# Revit family: NBS_WallgateLtd_WlHngUrnls_CWU-01
name_source: partatom
category: Plumbing Fixtures
revit_build: Autodesk Revit 2014 (Build: 20130709_2115(x64)
units: mm (PartAtom-declared; Revit-internal decimal feet)

## types (1)
- CWU-01
    AssetType = Fixed
    BIMObjectName = NBS_WallgateLtd_WallHungWashUrinal_CWU-01
    BowlUrinalMaterial = NBS_Concept
    ColourOptions = MA - Thames, MAH - Frost, MAW - White, MC - Bluestone, MCA - Aubergine, MCB - Diamantina, MCC - Black, MCD - Orange, MCE - Pink, MO - Slate, MS - Hyco, MCJ - Light Grey, MCF - NHS Blue
    ConnectingDimensions = BS EN 80
    Description = Anti-vandal solid surface urinal with 150 mm through wall concealed waste
    DrainSize = 32 mm  [stored 0.104987 ft]
    Durability = Compliant to Grade 5
    DurationUnit = year
    FixingMaterial = NBS_Concept
    IfcExportAs = IfcSanitaryTerminalType
    IfcExportType = URINAL
    IntegralAccessoryOptions = CWUS Urinal Shroud, CIST Cisterns, DFKIT-CWU Potable Direct Flush Valves, WDC Electronic Controllers, CWD Urinal Dividers
    ManufacturerName = Wallgate Ltd
    ManufacturerURL = www.wallgate.com
    Material = Solid surface
    MaterialsBody = Solid surface
    MaximumWallThickness = 150 mm  [stored 0.492126 ft]
    ModelNumber = CWU-01
    NBSCertification = www.nationalbimlibrary.com/cert/ai5dgyx3
    NBSDescription = Wall hung urinals
    NBSReference = 45-35-70/350
    Name = WallHungUrinals_CWU-01_WallgateLtd
    NominalDepth = 270 mm
    NominalHeight = 435 mm
    NominalLength = 0 mm  [stored 0 ft]
    NominalWidth = 310 mm
    OperationCompatibility = DFKIT-CWU Potable Direct Flush Valves, WDC Electronic Controllers
    ProductInformation = www.wallgate.com/products/urinals-and-accessories/cwu-urinal-shroud-dividers
    Size = 435 x 310 x 270 mm
    SpilloverLevel = 109 mm
    Standards = BS 5520
    ThirdPartyCertification = WRAS approved
    Uniclass2 = 45-31-93/482
    UrinalMaterial = High-grade solid surface material
    UrinalType = Bowl
    Version = 1
    WallThicknessOptions = Upto 150 mm
    WarrantyDurationParts = 1
    WarrantyDurationUnit = year
    WaterSupplyOverflowAndWasteHolesWaterSupply = Top supply hole
    WaterSupplyOverflowAndWasteOverflow = None
    WaterSupplyOverflowAndWasteWaste = 150 mm through wall concealed outlet
    Weight = 10.0 kg

note: [stored X ft] marks values corroborated as IEEE doubles in the binary element streams (Revit-internal decimal feet)

## geometry (parser evidence)
native form markers: Sweep x2
no freeform markers — native parametric forms only
